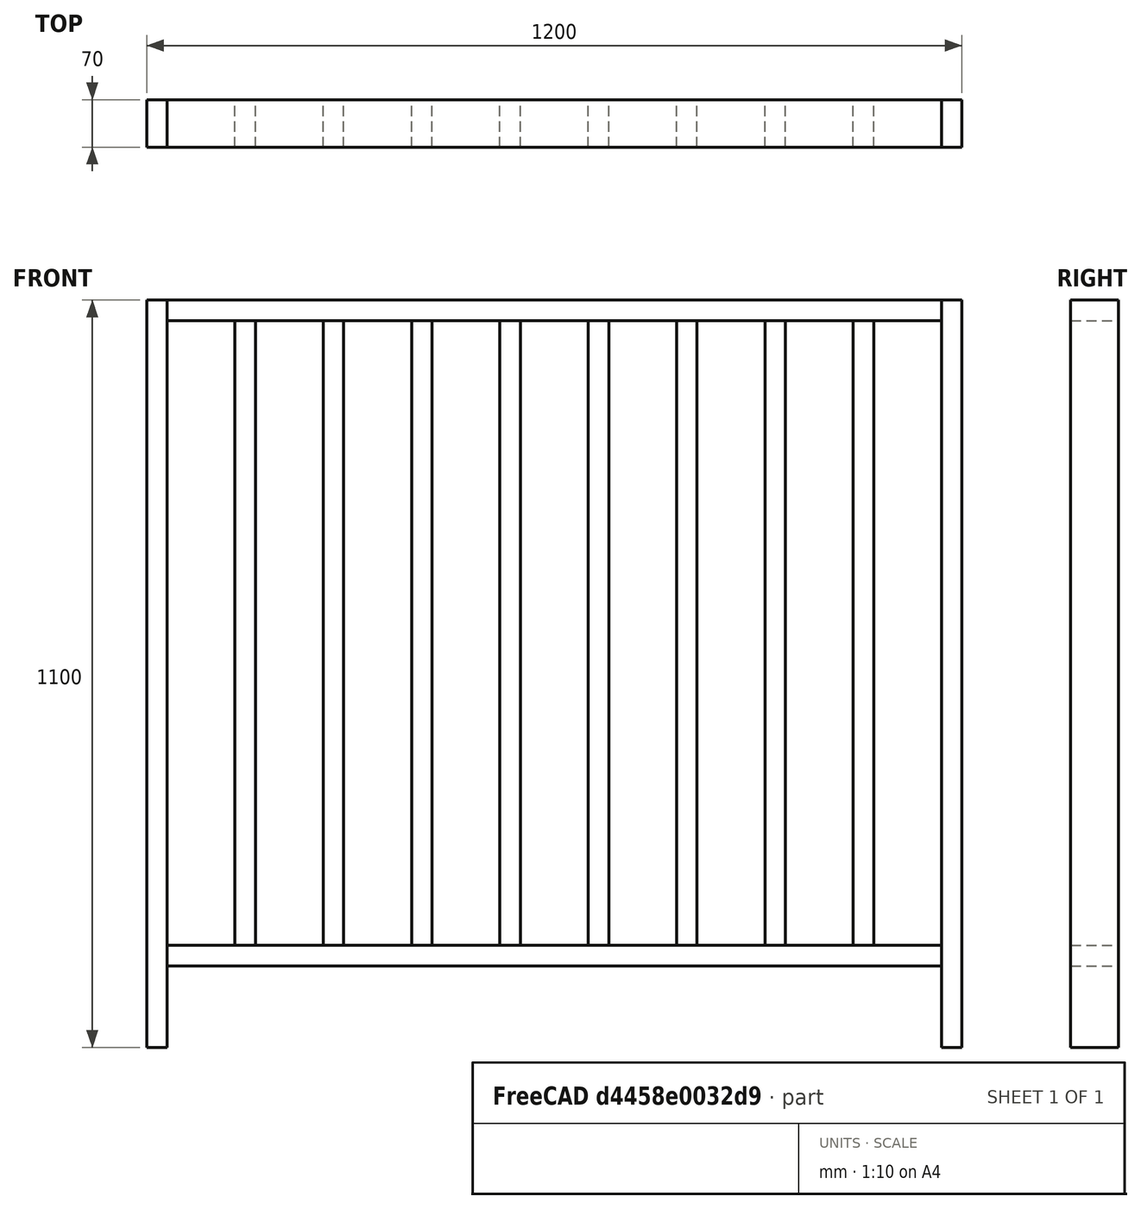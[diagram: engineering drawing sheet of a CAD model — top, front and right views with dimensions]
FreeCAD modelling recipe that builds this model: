
FCSTD DOCUMENT  (FreeCAD 0.18R16146 (Git))
Label: guarda-corpo-grade
License: All rights reserved
LicenseURL: http://en.wikipedia.org/wiki/All_rights_reserved
objects: Part::Box×5, Spreadsheet::Sheet×1, Part::FeaturePython×1
note: 6 computed .brp shape members not serialized (recipe doc carries the construction recipe); baked Part::Feature solids carry a one-line shape summary decoded from their .brp

FEATURE [Spreadsheet::Sheet] Spreadsheet  label="medidas"
  cells = B1=altura (height); C1=frente (length); D1=profundidade (width); E1=z; F1=x; G1=y; H1=quantidade; A2=pe_direito_1; B2(pe_direito_1_height)=1100; C2(pe_direito_1_length)=30; D2(pe_direito_1_width)=70; E2(pe_direito_1_z)=0; F2(pe_direito_1_x)=0; G2(pe_direito_1_y)=0; H2=1; A3=pe_direito_2; B3(pe_direito_2_height)=1100; C3(pe_direito_2_length)=30; D3(pe_direito_2_width)=70; E3(pe_direito_2_z)=0; F3(pe_direito_2_x)=1170; G3(pe_direito_2_y)=0; H3=1; A4=travessa_inferior; B4(travessa_inferior_height)=30; C4(travessa_inferior_length)=1140; D4(travessa_inferior_width)=70; E4(travessa_inferior_z)=120; F4(travessa_inferior_x)=30; G4(travessa_inferior_y)=0; H4=1; A5=travessa_superior; B5(travessa_superior_height)=30; C5(travessa_superior_length)=1140; D5(travessa_superior_width)=70; E5(travessa_superior_z)=1070; F5(travessa_superior_x)=30; G5(travessa_superior_y)=0; H5=1; A6=palito_grade; B6(palito_grade_height)=920; C6(palito_grade_length)=30; D6(palito_grade_width)=70; E6(palito_grade_z)=0; F6(palito_grade_x)=0; G6(palito_grade_y)=0; H6=1; A7=palitos; E7(palitos_z)=150; F7(palitos_x)=130; G7(palitos_y)=0; H7(palitos_qty)=8
FEATURE [Part::Box] Box  label="pe_direito_1"
  AttacherType = Attacher::AttachEngine3D
  Height = 1100
  Length = 30
  Width = 70
  expr: Placement.Base.z = medidas.pe_direito_1_z
  expr: Placement.Base.y = medidas.pe_direito_1_y
  expr: Placement.Base.x = medidas.pe_direito_1_x
  expr: Height = medidas.pe_direito_1_height
  expr: Width = medidas.pe_direito_1_width
  expr: Length = medidas.pe_direito_1_length
FEATURE [Part::Box] Box001  label="pe_direito_2"
  AttacherType = Attacher::AttachEngine3D
  Height = 1100
  Length = 30
  Placement = pos=(1170,0,0) rot=(0,0,1;0rad)
  Width = 70
  expr: Placement.Base.z = medidas.pe_direito_2_z
  expr: Placement.Base.y = medidas.pe_direito_2_y
  expr: Placement.Base.x = medidas.pe_direito_2_x
  expr: Height = medidas.pe_direito_2_height
  expr: Width = medidas.pe_direito_2_width
  expr: Length = medidas.pe_direito_2_length
FEATURE [Part::Box] Box002  label="travessa_inferior"
  AttacherType = Attacher::AttachEngine3D
  Height = 30
  Length = 1140
  Placement = pos=(30,0,120) rot=(0,0,1;0rad)
  Width = 70
  expr: Placement.Base.z = medidas.travessa_inferior_z
  expr: Placement.Base.y = medidas.travessa_inferior_y
  expr: Placement.Base.x = medidas.travessa_inferior_x
  expr: Height = medidas.travessa_inferior_height
  expr: Width = medidas.travessa_inferior_width
  expr: Length = medidas.travessa_inferior_length
FEATURE [Part::Box] Box003  label="travessa_superior"
  AttacherType = Attacher::AttachEngine3D
  Height = 30
  Length = 1140
  Placement = pos=(30,0,1070) rot=(0,0,1;0rad)
  Width = 70
  expr: Placement.Base.z = medidas.travessa_superior_z
  expr: Placement.Base.y = medidas.travessa_superior_y
  expr: Placement.Base.x = medidas.travessa_superior_x
  expr: Height = medidas.travessa_superior_height
  expr: Width = medidas.travessa_superior_width
  expr: Length = medidas.travessa_superior_length
FEATURE [Part::Box] Box004  label="palito_grade"
  AttacherType = Attacher::AttachEngine3D
  Height = 920
  Length = 30
  Width = 70
  expr: Placement.Base.z = medidas.palito_grade_z
  expr: Placement.Base.y = medidas.palito_grade_y
  expr: Placement.Base.x = medidas.palito_grade_x
  expr: Height = medidas.palito_grade_height
  expr: Width = medidas.palito_grade_width
  expr: Length = medidas.palito_grade_length
FEATURE [Part::FeaturePython] Array  label="palitos"  # Draft array (typed FeaturePython)
  Angle = 360
  ArrayType = 0
  Axis = (0,0,1)
  Base = -> Box004
  Center = (0,0,0)
  Fuse = false
  IntervalAxis = (0,0,0)
  IntervalX = (130,0,0)
  IntervalY = (0,1,0)
  IntervalZ = (0,0,1)
  NumberPolar = 1
  NumberX = 8
  NumberY = 1
  NumberZ = 1
  Placement = pos=(130,0,150) rot=(0,0,1;0rad)
  expr: NumberX = medidas.palitos_qty
  expr: Placement.Base.z = medidas.palitos_z
  expr: Placement.Base.y = medidas.palitos_y
  expr: Placement.Base.x = medidas.palitos_x
